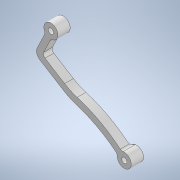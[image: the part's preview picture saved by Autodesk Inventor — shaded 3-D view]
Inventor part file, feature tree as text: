
AUTODESK INVENTOR PART (.ipt)
format: ipt  version: 2020 (Build 240168000, 168)  size: 178,176 bytes
history: native  units: mm
features: sketch x3, other x3, extrude x2, fillet x2, reference x2, projected_geometry x2, hole x1
ambient origin geometry x8: Origin, YZ Plane, XZ Plane, XY Plane, X Axis, Y Axis, Z Axis, Center Point
bodies: Solid1 (feature_tree)
feature tree (15):
  extrude  "Extrusion1"  Depth=27.0mm
  hole  "Hole1"  [1 undecoded]
  extrude  "Extrusion2"  Depth=1.0mm
  fillet  "Fillet1"  Radius=70.0mm
  fillet  "Fillet2"  Radius=7.0mm
  sketch  "Sketch1"  dims[d0=8.0mm d1=27.0mm]
  reference  "Reference1"
  reference  "Reference2"
  sketch  "Sketch2"  dims[d3=8.0mm d4=3.5mm]
  projected_geometry  "Projected Loop1"
  sketch  "Sketch3"  dims[d6=3.5mm d7=70.0mm d8=70.0mm d9=7.0mm d10=0.0mm d11=3.0mm d12=6.0mm d13=4.0mm d14=2.0mm d15=90.0deg d16=8.0mm d17=0.0mm d18=8.0mm d19=8.0mm d20=2.0mm d21=0.0mm d22=2.0mm d23=1.0mm]
  projected_geometry  "Projected Loop2"
  parser-record x1  (decoder bookkeeping rows leaked as tree rows — omitted from the tree; the rows remain in map.json)
  other  "leg_1.iam"
  other  "leg_holder_2:1"
note: 1 required parameter value undecoded (feature->parameter linkage not recoverable at this tier; creation-order binding heuristic only, values carry confidence <= 0.55)
note: 1 file-system path scrubbed to <path> (originals preserved in map.json)
